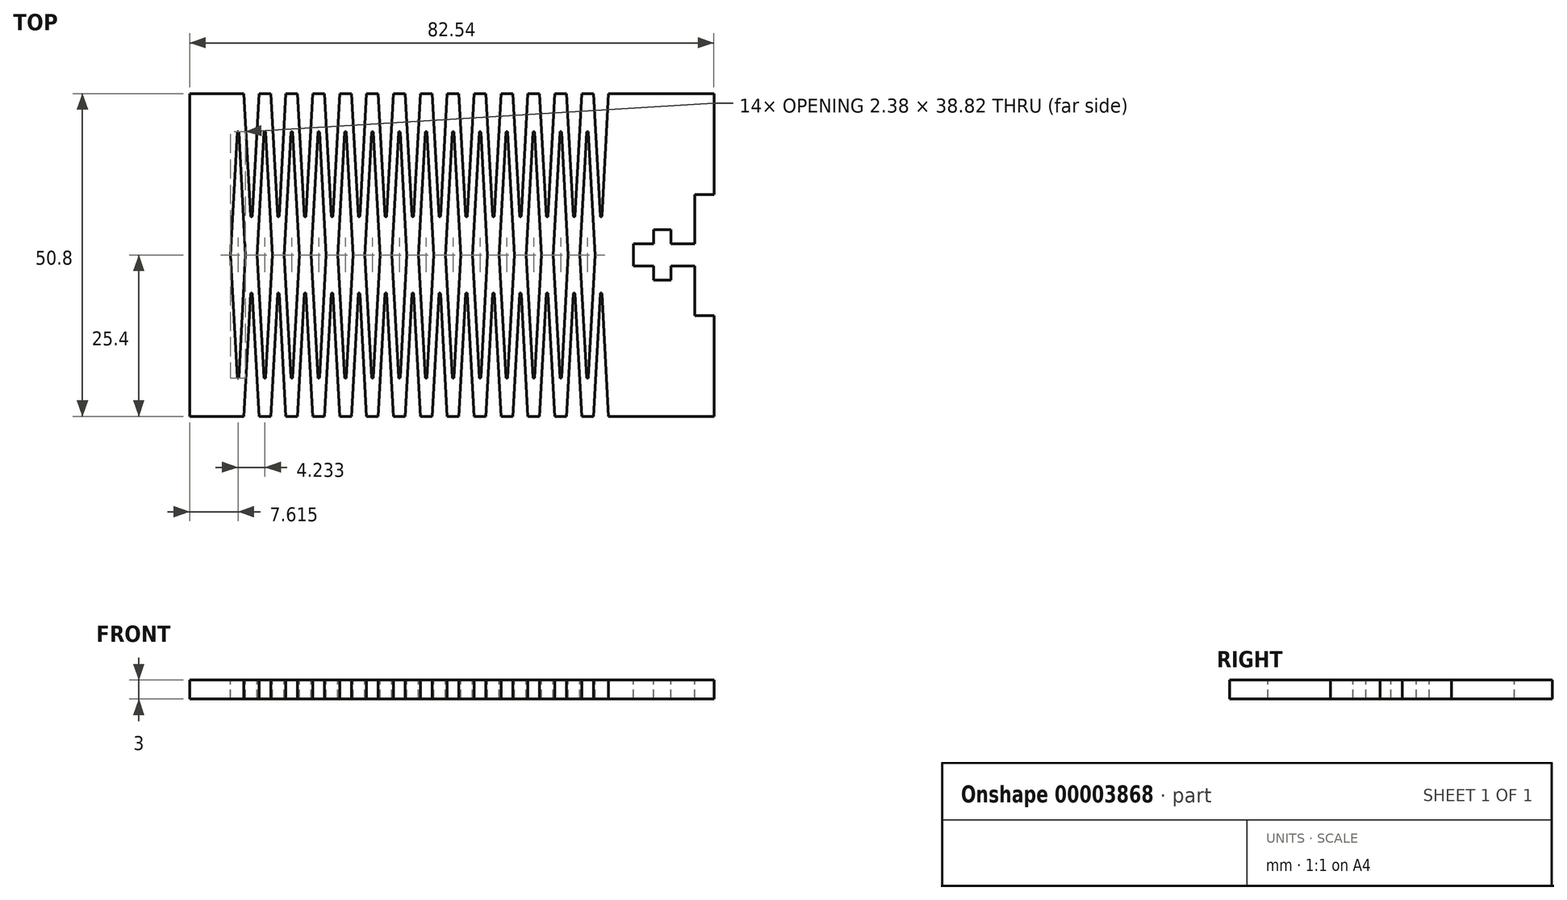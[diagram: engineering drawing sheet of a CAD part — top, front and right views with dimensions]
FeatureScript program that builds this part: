
annotation { "Feature Type Name" : "Feature", "Feature Type Description" : "" }
export const myFeature = defineFeature(function(context is Context, id is Id, definition is map)
    precondition{}
    {
        {
            var Q0;
            Q0=qCreatedBy(makeId("Top.planeOp"),FACE);
            var sketch = newSketch(context, id + "F0", { "sketchPlane" : qUnion([Q0])});
            skLineSegment(sketch, "E0.rect.bottom", {"start": v(41.28, 25.4) * mm, "end": v(-41.28, 25.4) * mm});
            skLineSegment(sketch, "E0.rect.top", {"start": v(41.28, -25.4) * mm, "end": v(-41.28, -25.4) * mm});
            skLineSegment(sketch, "E0.rect.left", {"start": v(41.28, 25.4) * mm, "end": v(41.28, -25.4) * mm});
            skLineSegment(sketch, "E0.rect.right", {"start": v(-41.28, 25.4) * mm, "end": v(-41.28, -25.4) * mm});
            skPoint(sketch, "E0.rect.middle", {"position": v(0, 0) * mm});
            skSolve(sketch);
        }
        {
            var Q0;
            Q0=makeQuery(id+"F0.imprint","IMPRINT",FACE,{"disambiguationData":[TD([[makeQuery(id+"F0.imprint","IMPRINT",EDGE,{"derivedFrom":sQuery(id+"F0.wireOp",EDGE,"E0.rect.bottom")}),1.0]])]});
            extrude(context, id + "F1", {"entities" : qUnion([Q0]), "depth" : 3 * mm});
        }
        {
            var Q0;
            Q0=makeQuery(id+"F1.opExtrude","CAP_FACE",FACE,{"disambiguationData":[OSD([sQuery(id+"F0.wireOp",EDGE,"E0.rect.bottom"),sQuery(id+"F0.wireOp",EDGE,"E0.rect.top"),sQuery(id+"F0.wireOp",EDGE,"E0.rect.left"),sQuery(id+"F0.wireOp",EDGE,"E0.rect.right")])],"isStart":false});
            var sketch = newSketch(context, id + "F2", { "sketchPlane" : qUnion([Q0])});
            skLineSegment(sketch, "E1.rect.bottom", {"start": v(38.28, 9.53) * mm, "end": v(41.28, 9.53) * mm});
            skLineSegment(sketch, "E1.rect.top", {"start": v(38.28, -9.53) * mm, "end": v(41.28, -9.53) * mm});
            skLineSegment(sketch, "E1.rect.right", {"start": v(41.28, 9.52) * mm, "end": v(41.28, -9.53) * mm});
            skPoint(sketch, "E1.rect.middle", {"position": v(39.78, 0) * mm});
            skLineSegment(sketch, "E2", {"start": v(38.28, 9.53) * mm, "end": v(38.28, 1.75) * mm});
            skLineSegment(sketch, "E3", {"start": v(38.28, 1.75) * mm, "end": v(34.53, 1.75) * mm});
            skLineSegment(sketch, "E4", {"start": v(34.53, 1.75) * mm, "end": v(34.53, 3.97) * mm});
            skLineSegment(sketch, "E5", {"start": v(34.53, 3.97) * mm, "end": v(31.75, 3.97) * mm});
            skLineSegment(sketch, "E6", {"start": v(31.75, 3.97) * mm, "end": v(31.75, 1.75) * mm});
            skLineSegment(sketch, "E7", {"start": v(31.75, 1.75) * mm, "end": v(28.58, 1.75) * mm});
            skLineSegment(sketch, "E8", {"start": v(28.58, 1.75) * mm, "end": v(28.58, 0) * mm});
            skLineSegment(sketch, "E9", {"start": v(41.28, 0) * mm, "end": v(11.15, 0) * mm, "construction": true});
            skLineSegment(sketch, "E10.0.MirrorCS", {"start": v(38.28, -9.53) * mm, "end": v(38.28, -1.75) * mm});
            skLineSegment(sketch, "E11.0.MirrorCS", {"start": v(38.28, -1.75) * mm, "end": v(34.53, -1.75) * mm});
            skLineSegment(sketch, "E12.0.MirrorCS", {"start": v(34.53, -1.75) * mm, "end": v(34.53, -3.97) * mm});
            skLineSegment(sketch, "E13.0.MirrorCS", {"start": v(34.53, -3.97) * mm, "end": v(31.75, -3.97) * mm});
            skLineSegment(sketch, "E14.0.MirrorCS", {"start": v(31.75, -3.97) * mm, "end": v(31.75, -1.75) * mm});
            skLineSegment(sketch, "E15.0.MirrorCS", {"start": v(31.75, -1.75) * mm, "end": v(28.58, -1.75) * mm});
            skLineSegment(sketch, "E16.0.MirrorCS", {"start": v(28.58, -1.75) * mm, "end": v(28.58, 0) * mm});
            skLineSegment(sketch, "E17", {"start": v(23.62, 6.1) * mm, "end": v(24.69, 25.4) * mm});
            skLineSegment(sketch, "E18", {"start": v(24.69, 25.4) * mm, "end": v(22.3, 25.4) * mm});
            skLineSegment(sketch, "E19", {"start": v(22.3, 25.4) * mm, "end": v(23.37, 6.1) * mm});
            skPoint(sketch, "E20.visualSharp", {"position": v(23.5, 3.81) * mm});
            skArc(sketch, "E20.filletArc", {"start": v(23.37, 6.1) * mm, "mid": v(23.5, 5.99) * mm, "end": v(23.62, 6.1) * mm});
            skLineSegment(sketch, "E21.0.MirrorCS", {"start": v(22.3, -25.4) * mm, "end": v(23.37, -6.1) * mm});
            skLineSegment(sketch, "E22.0.MirrorCS", {"start": v(23.62, -6.1) * mm, "end": v(24.69, -25.4) * mm});
            skLineSegment(sketch, "E23.0.MirrorCS", {"start": v(24.69, -25.4) * mm, "end": v(22.3, -25.4) * mm});
            skArc(sketch, "E24.0.MirrorCS", {"start": v(23.37, -6.1) * mm, "mid": v(23.5, -5.99) * mm, "end": v(23.62, -6.1) * mm});
            skLineSegment(sketch, "E25.1.0.0", {"start": v(18.07, 25.4) * mm, "end": v(19.13, 6.1) * mm});
            skLineSegment(sketch, "E25.1.0.1", {"start": v(19.39, 6.1) * mm, "end": v(20.45, 25.4) * mm});
            skLineSegment(sketch, "E25.1.0.2", {"start": v(20.45, 25.4) * mm, "end": v(18.07, 25.4) * mm});
            skLineSegment(sketch, "E25.1.0.3", {"start": v(18.07, -25.4) * mm, "end": v(19.13, -6.1) * mm});
            skLineSegment(sketch, "E25.1.0.4", {"start": v(19.39, -6.1) * mm, "end": v(20.45, -25.4) * mm});
            skLineSegment(sketch, "E25.1.0.5", {"start": v(20.45, -25.4) * mm, "end": v(18.07, -25.4) * mm});
            skArc(sketch, "E25.1.0.6", {"start": v(19.13, -6.1) * mm, "mid": v(19.26, -5.99) * mm, "end": v(19.39, -6.1) * mm});
            skArc(sketch, "E25.1.0.7", {"start": v(19.13, 6.1) * mm, "mid": v(19.26, 5.99) * mm, "end": v(19.39, 6.1) * mm});
            skLineSegment(sketch, "E25.2.0.0", {"start": v(13.84, 25.4) * mm, "end": v(14.9, 6.1) * mm});
            skLineSegment(sketch, "E25.2.0.1", {"start": v(15.16, 6.1) * mm, "end": v(16.22, 25.4) * mm});
            skLineSegment(sketch, "E25.2.0.2", {"start": v(16.22, 25.4) * mm, "end": v(13.84, 25.4) * mm});
            skLineSegment(sketch, "E25.2.0.3", {"start": v(13.84, -25.4) * mm, "end": v(14.9, -6.1) * mm});
            skLineSegment(sketch, "E25.2.0.4", {"start": v(15.16, -6.1) * mm, "end": v(16.22, -25.4) * mm});
            skLineSegment(sketch, "E25.2.0.5", {"start": v(16.22, -25.4) * mm, "end": v(13.84, -25.4) * mm});
            skArc(sketch, "E25.2.0.6", {"start": v(14.9, -6.1) * mm, "mid": v(15.03, -5.99) * mm, "end": v(15.16, -6.1) * mm});
            skArc(sketch, "E25.2.0.7", {"start": v(14.9, 6.1) * mm, "mid": v(15.03, 5.99) * mm, "end": v(15.16, 6.1) * mm});
            skLineSegment(sketch, "E25.direction1", {"start": v(23.37, 6.1) * mm, "end": v(19.13, 6.1) * mm, "construction": true});
            skLineSegment(sketch, "E26.0.3.0", {"start": v(9.6, 25.4) * mm, "end": v(10.67, 6.1) * mm});
            skLineSegment(sketch, "E26.3.3.0", {"start": v(10.92, 6.1) * mm, "end": v(11.99, 25.4) * mm});
            skLineSegment(sketch, "E26.6.3.0", {"start": v(11.99, 25.4) * mm, "end": v(9.6, 25.4) * mm});
            skLineSegment(sketch, "E26.9.3.0", {"start": v(9.6, -25.4) * mm, "end": v(10.67, -6.1) * mm});
            skLineSegment(sketch, "E26.12.3.0", {"start": v(10.92, -6.1) * mm, "end": v(11.99, -25.4) * mm});
            skLineSegment(sketch, "E26.15.3.0", {"start": v(11.99, -25.4) * mm, "end": v(9.6, -25.4) * mm});
            skArc(sketch, "E26.18.3.0", {"start": v(10.67, -6.1) * mm, "mid": v(10.8, -5.99) * mm, "end": v(10.92, -6.1) * mm});
            skArc(sketch, "E26.22.3.0", {"start": v(10.67, 6.1) * mm, "mid": v(10.8, 5.99) * mm, "end": v(10.92, 6.1) * mm});
            skLineSegment(sketch, "E26.0.4.0", {"start": v(5.37, 25.4) * mm, "end": v(6.43, 6.1) * mm});
            skLineSegment(sketch, "E26.3.4.0", {"start": v(6.69, 6.1) * mm, "end": v(7.75, 25.4) * mm});
            skLineSegment(sketch, "E26.6.4.0", {"start": v(7.75, 25.4) * mm, "end": v(5.37, 25.4) * mm});
            skLineSegment(sketch, "E26.9.4.0", {"start": v(5.37, -25.4) * mm, "end": v(6.43, -6.1) * mm});
            skLineSegment(sketch, "E26.12.4.0", {"start": v(6.69, -6.1) * mm, "end": v(7.75, -25.4) * mm});
            skLineSegment(sketch, "E26.15.4.0", {"start": v(7.75, -25.4) * mm, "end": v(5.37, -25.4) * mm});
            skArc(sketch, "E26.18.4.0", {"start": v(6.43, -6.1) * mm, "mid": v(6.56, -5.99) * mm, "end": v(6.69, -6.1) * mm});
            skArc(sketch, "E26.22.4.0", {"start": v(6.43, 6.1) * mm, "mid": v(6.56, 5.99) * mm, "end": v(6.69, 6.1) * mm});
            skLineSegment(sketch, "E26.0.5.0", {"start": v(1.14, 25.4) * mm, "end": v(2.2, 6.1) * mm});
            skLineSegment(sketch, "E26.3.5.0", {"start": v(2.46, 6.1) * mm, "end": v(3.52, 25.4) * mm});
            skLineSegment(sketch, "E26.6.5.0", {"start": v(3.52, 25.4) * mm, "end": v(1.14, 25.4) * mm});
            skLineSegment(sketch, "E26.9.5.0", {"start": v(1.14, -25.4) * mm, "end": v(2.2, -6.1) * mm});
            skLineSegment(sketch, "E26.12.5.0", {"start": v(2.46, -6.1) * mm, "end": v(3.52, -25.4) * mm});
            skLineSegment(sketch, "E26.15.5.0", {"start": v(3.52, -25.4) * mm, "end": v(1.14, -25.4) * mm});
            skArc(sketch, "E26.18.5.0", {"start": v(2.2, -6.1) * mm, "mid": v(2.33, -5.99) * mm, "end": v(2.46, -6.1) * mm});
            skArc(sketch, "E26.22.5.0", {"start": v(2.2, 6.1) * mm, "mid": v(2.33, 5.99) * mm, "end": v(2.46, 6.1) * mm});
            skLineSegment(sketch, "E26.0.6.0", {"start": v(-3.1, 25.4) * mm, "end": v(-2.03, 6.1) * mm});
            skLineSegment(sketch, "E26.3.6.0", {"start": v(-1.78, 6.1) * mm, "end": v(-0.71, 25.4) * mm});
            skLineSegment(sketch, "E26.6.6.0", {"start": v(-0.71, 25.4) * mm, "end": v(-3.1, 25.4) * mm});
            skLineSegment(sketch, "E26.9.6.0", {"start": v(-3.1, -25.4) * mm, "end": v(-2.03, -6.1) * mm});
            skLineSegment(sketch, "E26.12.6.0", {"start": v(-1.78, -6.1) * mm, "end": v(-0.71, -25.4) * mm});
            skLineSegment(sketch, "E26.15.6.0", {"start": v(-0.71, -25.4) * mm, "end": v(-3.1, -25.4) * mm});
            skArc(sketch, "E26.18.6.0", {"start": v(-2.03, -6.1) * mm, "mid": v(-1.9, -5.99) * mm, "end": v(-1.78, -6.1) * mm});
            skArc(sketch, "E26.22.6.0", {"start": v(-2.03, 6.1) * mm, "mid": v(-1.9, 5.99) * mm, "end": v(-1.78, 6.1) * mm});
            skLineSegment(sketch, "E26.0.7.0", {"start": v(-7.33, 25.4) * mm, "end": v(-6.27, 6.1) * mm});
            skLineSegment(sketch, "E26.3.7.0", {"start": v(-6.01, 6.1) * mm, "end": v(-4.95, 25.4) * mm});
            skLineSegment(sketch, "E26.6.7.0", {"start": v(-4.95, 25.4) * mm, "end": v(-7.33, 25.4) * mm});
            skLineSegment(sketch, "E26.9.7.0", {"start": v(-7.33, -25.4) * mm, "end": v(-6.27, -6.1) * mm});
            skLineSegment(sketch, "E26.12.7.0", {"start": v(-6.01, -6.1) * mm, "end": v(-4.95, -25.4) * mm});
            skLineSegment(sketch, "E26.15.7.0", {"start": v(-4.95, -25.4) * mm, "end": v(-7.33, -25.4) * mm});
            skArc(sketch, "E26.18.7.0", {"start": v(-6.27, -6.1) * mm, "mid": v(-6.14, -5.99) * mm, "end": v(-6.01, -6.1) * mm});
            skArc(sketch, "E26.22.7.0", {"start": v(-6.27, 6.1) * mm, "mid": v(-6.14, 5.99) * mm, "end": v(-6.01, 6.1) * mm});
            skLineSegment(sketch, "E26.0.8.0", {"start": v(-11.56, 25.4) * mm, "end": v(-10.5, 6.1) * mm});
            skLineSegment(sketch, "E26.3.8.0", {"start": v(-10.24, 6.1) * mm, "end": v(-9.18, 25.4) * mm});
            skLineSegment(sketch, "E26.6.8.0", {"start": v(-9.18, 25.4) * mm, "end": v(-11.56, 25.4) * mm});
            skLineSegment(sketch, "E26.9.8.0", {"start": v(-11.56, -25.4) * mm, "end": v(-10.5, -6.1) * mm});
            skLineSegment(sketch, "E26.12.8.0", {"start": v(-10.24, -6.1) * mm, "end": v(-9.18, -25.4) * mm});
            skLineSegment(sketch, "E26.15.8.0", {"start": v(-9.18, -25.4) * mm, "end": v(-11.56, -25.4) * mm});
            skArc(sketch, "E26.18.8.0", {"start": v(-10.5, -6.1) * mm, "mid": v(-10.37, -5.99) * mm, "end": v(-10.24, -6.1) * mm});
            skArc(sketch, "E26.22.8.0", {"start": v(-10.5, 6.1) * mm, "mid": v(-10.37, 5.99) * mm, "end": v(-10.24, 6.1) * mm});
            skLineSegment(sketch, "E26.0.9.0", {"start": v(-15.8, 25.4) * mm, "end": v(-14.73, 6.1) * mm});
            skLineSegment(sketch, "E26.3.9.0", {"start": v(-14.48, 6.1) * mm, "end": v(-13.41, 25.4) * mm});
            skLineSegment(sketch, "E26.6.9.0", {"start": v(-13.41, 25.4) * mm, "end": v(-15.8, 25.4) * mm});
            skLineSegment(sketch, "E26.9.9.0", {"start": v(-15.8, -25.4) * mm, "end": v(-14.73, -6.1) * mm});
            skLineSegment(sketch, "E26.12.9.0", {"start": v(-14.48, -6.1) * mm, "end": v(-13.41, -25.4) * mm});
            skLineSegment(sketch, "E26.15.9.0", {"start": v(-13.41, -25.4) * mm, "end": v(-15.8, -25.4) * mm});
            skArc(sketch, "E26.18.9.0", {"start": v(-14.73, -6.1) * mm, "mid": v(-14.6, -5.99) * mm, "end": v(-14.48, -6.1) * mm});
            skArc(sketch, "E26.22.9.0", {"start": v(-14.73, 6.1) * mm, "mid": v(-14.6, 5.99) * mm, "end": v(-14.48, 6.1) * mm});
            skLineSegment(sketch, "E27.0.10.0", {"start": v(-20.03, 25.4) * mm, "end": v(-18.97, 6.1) * mm});
            skLineSegment(sketch, "E27.3.10.0", {"start": v(-18.71, 6.1) * mm, "end": v(-17.65, 25.4) * mm});
            skLineSegment(sketch, "E27.6.10.0", {"start": v(-17.65, 25.4) * mm, "end": v(-20.03, 25.4) * mm});
            skLineSegment(sketch, "E27.9.10.0", {"start": v(-20.03, -25.4) * mm, "end": v(-18.97, -6.1) * mm});
            skLineSegment(sketch, "E27.12.10.0", {"start": v(-18.71, -6.1) * mm, "end": v(-17.65, -25.4) * mm});
            skLineSegment(sketch, "E27.15.10.0", {"start": v(-17.65, -25.4) * mm, "end": v(-20.03, -25.4) * mm});
            skArc(sketch, "E27.18.10.0", {"start": v(-18.97, -6.1) * mm, "mid": v(-18.84, -5.99) * mm, "end": v(-18.71, -6.1) * mm});
            skArc(sketch, "E27.22.10.0", {"start": v(-18.97, 6.1) * mm, "mid": v(-18.84, 5.99) * mm, "end": v(-18.71, 6.1) * mm});
            skLineSegment(sketch, "E27.0.11.0", {"start": v(-24.26, 25.4) * mm, "end": v(-23.2, 6.1) * mm});
            skLineSegment(sketch, "E27.3.11.0", {"start": v(-22.94, 6.1) * mm, "end": v(-21.88, 25.4) * mm});
            skLineSegment(sketch, "E27.6.11.0", {"start": v(-21.88, 25.4) * mm, "end": v(-24.26, 25.4) * mm});
            skLineSegment(sketch, "E27.9.11.0", {"start": v(-24.26, -25.4) * mm, "end": v(-23.2, -6.1) * mm});
            skLineSegment(sketch, "E27.12.11.0", {"start": v(-22.94, -6.1) * mm, "end": v(-21.88, -25.4) * mm});
            skLineSegment(sketch, "E27.15.11.0", {"start": v(-21.88, -25.4) * mm, "end": v(-24.26, -25.4) * mm});
            skArc(sketch, "E27.18.11.0", {"start": v(-23.2, -6.1) * mm, "mid": v(-23.07, -5.99) * mm, "end": v(-22.94, -6.1) * mm});
            skArc(sketch, "E27.22.11.0", {"start": v(-23.2, 6.1) * mm, "mid": v(-23.07, 5.99) * mm, "end": v(-22.94, 6.1) * mm});
            skLineSegment(sketch, "E27.0.12.0", {"start": v(-28.5, 25.4) * mm, "end": v(-27.43, 6.1) * mm});
            skLineSegment(sketch, "E27.3.12.0", {"start": v(-27.18, 6.1) * mm, "end": v(-26.11, 25.4) * mm});
            skLineSegment(sketch, "E27.6.12.0", {"start": v(-26.11, 25.4) * mm, "end": v(-28.5, 25.4) * mm});
            skLineSegment(sketch, "E27.9.12.0", {"start": v(-28.5, -25.4) * mm, "end": v(-27.43, -6.1) * mm});
            skLineSegment(sketch, "E27.12.12.0", {"start": v(-27.18, -6.1) * mm, "end": v(-26.11, -25.4) * mm});
            skLineSegment(sketch, "E27.15.12.0", {"start": v(-26.11, -25.4) * mm, "end": v(-28.5, -25.4) * mm});
            skArc(sketch, "E27.18.12.0", {"start": v(-27.43, -6.1) * mm, "mid": v(-27.3, -5.99) * mm, "end": v(-27.18, -6.1) * mm});
            skArc(sketch, "E27.22.12.0", {"start": v(-27.43, 6.1) * mm, "mid": v(-27.3, 5.99) * mm, "end": v(-27.18, 6.1) * mm});
            skLineSegment(sketch, "E27.0.13.0", {"start": v(-32.73, 25.4) * mm, "end": v(-31.67, 6.1) * mm});
            skLineSegment(sketch, "E27.3.13.0", {"start": v(-31.41, 6.1) * mm, "end": v(-30.35, 25.4) * mm});
            skLineSegment(sketch, "E27.6.13.0", {"start": v(-30.35, 25.4) * mm, "end": v(-32.73, 25.4) * mm});
            skLineSegment(sketch, "E27.9.13.0", {"start": v(-32.73, -25.4) * mm, "end": v(-31.67, -6.1) * mm});
            skLineSegment(sketch, "E27.12.13.0", {"start": v(-31.41, -6.1) * mm, "end": v(-30.35, -25.4) * mm});
            skLineSegment(sketch, "E27.15.13.0", {"start": v(-30.35, -25.4) * mm, "end": v(-32.73, -25.4) * mm});
            skArc(sketch, "E27.18.13.0", {"start": v(-31.67, -6.1) * mm, "mid": v(-31.54, -5.99) * mm, "end": v(-31.41, -6.1) * mm});
            skArc(sketch, "E27.22.13.0", {"start": v(-31.67, 6.1) * mm, "mid": v(-31.54, 5.99) * mm, "end": v(-31.41, 6.1) * mm});
            skLineSegment(sketch, "E28", {"start": v(21.5, 19.3) * mm, "end": v(22.57, 0) * mm});
            skLineSegment(sketch, "E29", {"start": v(20.19, 0) * mm, "end": v(21.25, 19.3) * mm});
            skPoint(sketch, "E30.visualSharp", {"position": v(21.38, 21.59) * mm});
            skArc(sketch, "E30.filletArc", {"start": v(21.5, 19.3) * mm, "mid": v(21.38, 19.41) * mm, "end": v(21.25, 19.3) * mm});
            skLineSegment(sketch, "E31.0.MirrorCS", {"start": v(20.19, 0) * mm, "end": v(21.25, -19.3) * mm});
            skLineSegment(sketch, "E32.0.MirrorCS", {"start": v(21.5, -19.3) * mm, "end": v(22.57, 0) * mm});
            skArc(sketch, "E33.0.MirrorCS", {"start": v(21.5, -19.3) * mm, "mid": v(21.38, -19.41) * mm, "end": v(21.25, -19.3) * mm});
            skLineSegment(sketch, "E34.1.0.0", {"start": v(15.95, 0) * mm, "end": v(17.02, -19.3) * mm});
            skLineSegment(sketch, "E34.1.0.1", {"start": v(17.27, -19.3) * mm, "end": v(18.34, 0) * mm});
            skLineSegment(sketch, "E34.1.0.2", {"start": v(15.95, 0) * mm, "end": v(17.02, 19.3) * mm});
            skLineSegment(sketch, "E34.1.0.3", {"start": v(17.27, 19.3) * mm, "end": v(18.34, 0) * mm});
            skArc(sketch, "E34.1.0.4", {"start": v(17.27, 19.3) * mm, "mid": v(17.15, 19.41) * mm, "end": v(17.02, 19.3) * mm});
            skArc(sketch, "E34.1.0.5", {"start": v(17.27, -19.3) * mm, "mid": v(17.15, -19.41) * mm, "end": v(17.02, -19.3) * mm});
            skLineSegment(sketch, "E34.2.0.0", {"start": v(11.72, 0) * mm, "end": v(12.78, -19.3) * mm});
            skLineSegment(sketch, "E34.2.0.1", {"start": v(13.04, -19.3) * mm, "end": v(14.1, 0) * mm});
            skLineSegment(sketch, "E34.2.0.2", {"start": v(11.72, 0) * mm, "end": v(12.78, 19.3) * mm});
            skLineSegment(sketch, "E34.2.0.3", {"start": v(13.04, 19.3) * mm, "end": v(14.1, 0) * mm});
            skArc(sketch, "E34.2.0.4", {"start": v(13.04, 19.3) * mm, "mid": v(12.91, 19.41) * mm, "end": v(12.78, 19.3) * mm});
            skArc(sketch, "E34.2.0.5", {"start": v(13.04, -19.3) * mm, "mid": v(12.91, -19.41) * mm, "end": v(12.78, -19.3) * mm});
            skLineSegment(sketch, "E34.direction1", {"start": v(21.25, -19.3) * mm, "end": v(17.02, -19.3) * mm, "construction": true});
            skLineSegment(sketch, "E35.0.3.0", {"start": v(7.49, 0) * mm, "end": v(8.55, -19.3) * mm});
            skLineSegment(sketch, "E35.3.3.0", {"start": v(8.8, -19.3) * mm, "end": v(9.87, 0) * mm});
            skLineSegment(sketch, "E35.6.3.0", {"start": v(7.49, 0) * mm, "end": v(8.55, 19.3) * mm});
            skLineSegment(sketch, "E35.9.3.0", {"start": v(8.8, 19.3) * mm, "end": v(9.87, 0) * mm});
            skArc(sketch, "E35.12.3.0", {"start": v(8.8, 19.3) * mm, "mid": v(8.68, 19.41) * mm, "end": v(8.55, 19.3) * mm});
            skArc(sketch, "E35.16.3.0", {"start": v(8.8, -19.3) * mm, "mid": v(8.68, -19.41) * mm, "end": v(8.55, -19.3) * mm});
            skLineSegment(sketch, "E35.0.4.0", {"start": v(3.25, 0) * mm, "end": v(4.32, -19.3) * mm});
            skLineSegment(sketch, "E35.3.4.0", {"start": v(4.57, -19.3) * mm, "end": v(5.64, 0) * mm});
            skLineSegment(sketch, "E35.6.4.0", {"start": v(3.25, 0) * mm, "end": v(4.32, 19.3) * mm});
            skLineSegment(sketch, "E35.9.4.0", {"start": v(4.57, 19.3) * mm, "end": v(5.64, 0) * mm});
            skArc(sketch, "E35.12.4.0", {"start": v(4.57, 19.3) * mm, "mid": v(4.45, 19.41) * mm, "end": v(4.32, 19.3) * mm});
            skArc(sketch, "E35.16.4.0", {"start": v(4.57, -19.3) * mm, "mid": v(4.45, -19.41) * mm, "end": v(4.32, -19.3) * mm});
            skLineSegment(sketch, "E35.0.5.0", {"start": v(-0.98, 0) * mm, "end": v(0.08, -19.3) * mm});
            skLineSegment(sketch, "E35.3.5.0", {"start": v(0.34, -19.3) * mm, "end": v(1.4, 0) * mm});
            skLineSegment(sketch, "E35.6.5.0", {"start": v(-0.98, 0) * mm, "end": v(0.08, 19.3) * mm});
            skLineSegment(sketch, "E35.9.5.0", {"start": v(0.34, 19.3) * mm, "end": v(1.4, 0) * mm});
            skArc(sketch, "E35.12.5.0", {"start": v(0.34, 19.3) * mm, "mid": v(0.21, 19.41) * mm, "end": v(0.08, 19.3) * mm});
            skArc(sketch, "E35.16.5.0", {"start": v(0.34, -19.3) * mm, "mid": v(0.21, -19.41) * mm, "end": v(0.08, -19.3) * mm});
            skLineSegment(sketch, "E35.0.6.0", {"start": v(-5.21, 0) * mm, "end": v(-4.15, -19.3) * mm});
            skLineSegment(sketch, "E35.3.6.0", {"start": v(-3.9, -19.3) * mm, "end": v(-2.83, 0) * mm});
            skLineSegment(sketch, "E35.6.6.0", {"start": v(-5.21, 0) * mm, "end": v(-4.15, 19.3) * mm});
            skLineSegment(sketch, "E35.9.6.0", {"start": v(-3.9, 19.3) * mm, "end": v(-2.83, 0) * mm});
            skArc(sketch, "E35.12.6.0", {"start": v(-3.9, 19.3) * mm, "mid": v(-4.02, 19.41) * mm, "end": v(-4.15, 19.3) * mm});
            skArc(sketch, "E35.16.6.0", {"start": v(-3.9, -19.3) * mm, "mid": v(-4.02, -19.41) * mm, "end": v(-4.15, -19.3) * mm});
            skLineSegment(sketch, "E35.0.7.0", {"start": v(-9.45, 0) * mm, "end": v(-8.38, -19.3) * mm});
            skLineSegment(sketch, "E35.3.7.0", {"start": v(-8.13, -19.3) * mm, "end": v(-7.06, 0) * mm});
            skLineSegment(sketch, "E35.6.7.0", {"start": v(-9.45, 0) * mm, "end": v(-8.38, 19.3) * mm});
            skLineSegment(sketch, "E35.9.7.0", {"start": v(-8.13, 19.3) * mm, "end": v(-7.06, 0) * mm});
            skArc(sketch, "E35.12.7.0", {"start": v(-8.13, 19.3) * mm, "mid": v(-8.25, 19.41) * mm, "end": v(-8.38, 19.3) * mm});
            skArc(sketch, "E35.16.7.0", {"start": v(-8.13, -19.3) * mm, "mid": v(-8.25, -19.41) * mm, "end": v(-8.38, -19.3) * mm});
            skLineSegment(sketch, "E35.0.8.0", {"start": v(-13.68, 0) * mm, "end": v(-12.62, -19.3) * mm});
            skLineSegment(sketch, "E35.3.8.0", {"start": v(-12.36, -19.3) * mm, "end": v(-11.3, 0) * mm});
            skLineSegment(sketch, "E35.6.8.0", {"start": v(-13.68, 0) * mm, "end": v(-12.62, 19.3) * mm});
            skLineSegment(sketch, "E35.9.8.0", {"start": v(-12.36, 19.3) * mm, "end": v(-11.3, 0) * mm});
            skArc(sketch, "E35.12.8.0", {"start": v(-12.36, 19.3) * mm, "mid": v(-12.49, 19.41) * mm, "end": v(-12.62, 19.3) * mm});
            skArc(sketch, "E35.16.8.0", {"start": v(-12.36, -19.3) * mm, "mid": v(-12.49, -19.41) * mm, "end": v(-12.62, -19.3) * mm});
            skLineSegment(sketch, "E35.0.9.0", {"start": v(-17.91, 0) * mm, "end": v(-16.85, -19.3) * mm});
            skLineSegment(sketch, "E35.3.9.0", {"start": v(-16.6, -19.3) * mm, "end": v(-15.53, 0) * mm});
            skLineSegment(sketch, "E35.6.9.0", {"start": v(-17.91, 0) * mm, "end": v(-16.85, 19.3) * mm});
            skLineSegment(sketch, "E35.9.9.0", {"start": v(-16.6, 19.3) * mm, "end": v(-15.53, 0) * mm});
            skArc(sketch, "E35.12.9.0", {"start": v(-16.6, 19.3) * mm, "mid": v(-16.72, 19.41) * mm, "end": v(-16.85, 19.3) * mm});
            skArc(sketch, "E35.16.9.0", {"start": v(-16.6, -19.3) * mm, "mid": v(-16.72, -19.41) * mm, "end": v(-16.85, -19.3) * mm});
            skLineSegment(sketch, "E35.0.10.0", {"start": v(-22.15, 0) * mm, "end": v(-21.08, -19.3) * mm});
            skLineSegment(sketch, "E35.3.10.0", {"start": v(-20.83, -19.3) * mm, "end": v(-19.76, 0) * mm});
            skLineSegment(sketch, "E35.6.10.0", {"start": v(-22.15, 0) * mm, "end": v(-21.08, 19.3) * mm});
            skLineSegment(sketch, "E35.9.10.0", {"start": v(-20.83, 19.3) * mm, "end": v(-19.76, 0) * mm});
            skArc(sketch, "E35.12.10.0", {"start": v(-20.83, 19.3) * mm, "mid": v(-20.95, 19.41) * mm, "end": v(-21.08, 19.3) * mm});
            skArc(sketch, "E35.16.10.0", {"start": v(-20.83, -19.3) * mm, "mid": v(-20.95, -19.41) * mm, "end": v(-21.08, -19.3) * mm});
            skLineSegment(sketch, "E35.0.11.0", {"start": v(-26.38, 0) * mm, "end": v(-25.32, -19.3) * mm});
            skLineSegment(sketch, "E35.3.11.0", {"start": v(-25.06, -19.3) * mm, "end": v(-24, 0) * mm});
            skLineSegment(sketch, "E35.6.11.0", {"start": v(-26.38, 0) * mm, "end": v(-25.32, 19.3) * mm});
            skLineSegment(sketch, "E35.9.11.0", {"start": v(-25.06, 19.3) * mm, "end": v(-24, 0) * mm});
            skArc(sketch, "E35.12.11.0", {"start": v(-25.06, 19.3) * mm, "mid": v(-25.19, 19.41) * mm, "end": v(-25.32, 19.3) * mm});
            skArc(sketch, "E35.16.11.0", {"start": v(-25.06, -19.3) * mm, "mid": v(-25.19, -19.41) * mm, "end": v(-25.32, -19.3) * mm});
            skLineSegment(sketch, "E35.0.12.0", {"start": v(-30.61, 0) * mm, "end": v(-29.55, -19.3) * mm});
            skLineSegment(sketch, "E35.3.12.0", {"start": v(-29.3, -19.3) * mm, "end": v(-28.23, 0) * mm});
            skLineSegment(sketch, "E35.6.12.0", {"start": v(-30.61, 0) * mm, "end": v(-29.55, 19.3) * mm});
            skLineSegment(sketch, "E35.9.12.0", {"start": v(-29.3, 19.3) * mm, "end": v(-28.23, 0) * mm});
            skArc(sketch, "E35.12.12.0", {"start": v(-29.3, 19.3) * mm, "mid": v(-29.42, 19.41) * mm, "end": v(-29.55, 19.3) * mm});
            skArc(sketch, "E35.16.12.0", {"start": v(-29.3, -19.3) * mm, "mid": v(-29.42, -19.41) * mm, "end": v(-29.55, -19.3) * mm});
            skLineSegment(sketch, "E35.0.13.0", {"start": v(-34.85, 0) * mm, "end": v(-33.78, -19.3) * mm});
            skLineSegment(sketch, "E35.3.13.0", {"start": v(-33.53, -19.3) * mm, "end": v(-32.46, 0) * mm});
            skLineSegment(sketch, "E35.6.13.0", {"start": v(-34.85, 0) * mm, "end": v(-33.78, 19.3) * mm});
            skLineSegment(sketch, "E35.9.13.0", {"start": v(-33.53, 19.3) * mm, "end": v(-32.46, 0) * mm});
            skArc(sketch, "E35.12.13.0", {"start": v(-33.53, 19.3) * mm, "mid": v(-33.65, 19.41) * mm, "end": v(-33.78, 19.3) * mm});
            skArc(sketch, "E35.16.13.0", {"start": v(-33.53, -19.3) * mm, "mid": v(-33.65, -19.41) * mm, "end": v(-33.78, -19.3) * mm});
            skSolve(sketch);
        }
        {
            var Q0;
            {Q0=qUnion([makeQuery(id+"F2.imprint","IMPRINT",FACE,{"disambiguationData":[TD([[makeQuery(id+"F2.imprint","IMPRINT",EDGE,{"derivedFrom":sQuery(id+"F2.wireOp",EDGE,"E1.rect.bottom")}),-1.0]])]}),makeQuery(id+"F2.imprint","IMPRINT",FACE,{"disambiguationData":[TD([[makeQuery(id+"F2.imprint","IMPRINT",EDGE,{"derivedFrom":sQuery(id+"F2.wireOp",EDGE,"E17")}),1.0]])]}),makeQuery(id+"F2.imprint","IMPRINT",FACE,{"disambiguationData":[TD([[makeQuery(id+"F2.imprint","IMPRINT",EDGE,{"derivedFrom":sQuery(id+"F2.wireOp",EDGE,"E21.0.MirrorCS")}),-1.0]])]}),makeQuery(id+"F2.imprint","IMPRINT",FACE,{"disambiguationData":[TD([[makeQuery(id+"F2.imprint","IMPRINT",EDGE,{"derivedFrom":sQuery(id+"F2.wireOp",EDGE,"E25.1.0.0")}),1.0]])]}),makeQuery(id+"F2.imprint","IMPRINT",FACE,{"disambiguationData":[TD([[makeQuery(id+"F2.imprint","IMPRINT",EDGE,{"derivedFrom":sQuery(id+"F2.wireOp",EDGE,"E25.1.0.3")}),-1.0]])]}),makeQuery(id+"F2.imprint","IMPRINT",FACE,{"disambiguationData":[TD([[makeQuery(id+"F2.imprint","IMPRINT",EDGE,{"derivedFrom":sQuery(id+"F2.wireOp",EDGE,"E25.2.0.0")}),1.0]])]}),makeQuery(id+"F2.imprint","IMPRINT",FACE,{"disambiguationData":[TD([[makeQuery(id+"F2.imprint","IMPRINT",EDGE,{"derivedFrom":sQuery(id+"F2.wireOp",EDGE,"E25.2.0.3")}),-1.0]])]}),makeQuery(id+"F2.imprint","IMPRINT",FACE,{"disambiguationData":[TD([[makeQuery(id+"F2.imprint","IMPRINT",EDGE,{"derivedFrom":sQuery(id+"F2.wireOp",EDGE,"E26.0.3.0")}),1.0]])]}),makeQuery(id+"F2.imprint","IMPRINT",FACE,{"disambiguationData":[TD([[makeQuery(id+"F2.imprint","IMPRINT",EDGE,{"derivedFrom":sQuery(id+"F2.wireOp",EDGE,"E26.9.3.0")}),-1.0]])]}),makeQuery(id+"F2.imprint","IMPRINT",FACE,{"disambiguationData":[TD([[makeQuery(id+"F2.imprint","IMPRINT",EDGE,{"derivedFrom":sQuery(id+"F2.wireOp",EDGE,"E26.0.4.0")}),1.0]])]}),makeQuery(id+"F2.imprint","IMPRINT",FACE,{"disambiguationData":[TD([[makeQuery(id+"F2.imprint","IMPRINT",EDGE,{"derivedFrom":sQuery(id+"F2.wireOp",EDGE,"E26.9.4.0")}),-1.0]])]}),makeQuery(id+"F2.imprint","IMPRINT",FACE,{"disambiguationData":[TD([[makeQuery(id+"F2.imprint","IMPRINT",EDGE,{"derivedFrom":sQuery(id+"F2.wireOp",EDGE,"E26.0.5.0")}),1.0]])]}),makeQuery(id+"F2.imprint","IMPRINT",FACE,{"disambiguationData":[TD([[makeQuery(id+"F2.imprint","IMPRINT",EDGE,{"derivedFrom":sQuery(id+"F2.wireOp",EDGE,"E26.9.5.0")}),-1.0]])]}),makeQuery(id+"F2.imprint","IMPRINT",FACE,{"disambiguationData":[TD([[makeQuery(id+"F2.imprint","IMPRINT",EDGE,{"derivedFrom":sQuery(id+"F2.wireOp",EDGE,"E26.0.6.0")}),1.0]])]}),makeQuery(id+"F2.imprint","IMPRINT",FACE,{"disambiguationData":[TD([[makeQuery(id+"F2.imprint","IMPRINT",EDGE,{"derivedFrom":sQuery(id+"F2.wireOp",EDGE,"E26.9.6.0")}),-1.0]])]}),makeQuery(id+"F2.imprint","IMPRINT",FACE,{"disambiguationData":[TD([[makeQuery(id+"F2.imprint","IMPRINT",EDGE,{"derivedFrom":sQuery(id+"F2.wireOp",EDGE,"E26.0.7.0")}),1.0]])]}),makeQuery(id+"F2.imprint","IMPRINT",FACE,{"disambiguationData":[TD([[makeQuery(id+"F2.imprint","IMPRINT",EDGE,{"derivedFrom":sQuery(id+"F2.wireOp",EDGE,"E26.9.7.0")}),-1.0]])]}),makeQuery(id+"F2.imprint","IMPRINT",FACE,{"disambiguationData":[TD([[makeQuery(id+"F2.imprint","IMPRINT",EDGE,{"derivedFrom":sQuery(id+"F2.wireOp",EDGE,"E26.0.8.0")}),1.0]])]}),makeQuery(id+"F2.imprint","IMPRINT",FACE,{"disambiguationData":[TD([[makeQuery(id+"F2.imprint","IMPRINT",EDGE,{"derivedFrom":sQuery(id+"F2.wireOp",EDGE,"E26.9.8.0")}),-1.0]])]}),makeQuery(id+"F2.imprint","IMPRINT",FACE,{"disambiguationData":[TD([[makeQuery(id+"F2.imprint","IMPRINT",EDGE,{"derivedFrom":sQuery(id+"F2.wireOp",EDGE,"E26.0.9.0")}),1.0]])]}),makeQuery(id+"F2.imprint","IMPRINT",FACE,{"disambiguationData":[TD([[makeQuery(id+"F2.imprint","IMPRINT",EDGE,{"derivedFrom":sQuery(id+"F2.wireOp",EDGE,"E26.9.9.0")}),-1.0]])]}),makeQuery(id+"F2.imprint","IMPRINT",FACE,{"disambiguationData":[TD([[makeQuery(id+"F2.imprint","IMPRINT",EDGE,{"derivedFrom":sQuery(id+"F2.wireOp",EDGE,"E27.0.10.0")}),1.0]])]}),makeQuery(id+"F2.imprint","IMPRINT",FACE,{"disambiguationData":[TD([[makeQuery(id+"F2.imprint","IMPRINT",EDGE,{"derivedFrom":sQuery(id+"F2.wireOp",EDGE,"E27.9.10.0")}),-1.0]])]}),makeQuery(id+"F2.imprint","IMPRINT",FACE,{"disambiguationData":[TD([[makeQuery(id+"F2.imprint","IMPRINT",EDGE,{"derivedFrom":sQuery(id+"F2.wireOp",EDGE,"E27.0.11.0")}),1.0]])]}),makeQuery(id+"F2.imprint","IMPRINT",FACE,{"disambiguationData":[TD([[makeQuery(id+"F2.imprint","IMPRINT",EDGE,{"derivedFrom":sQuery(id+"F2.wireOp",EDGE,"E27.9.11.0")}),-1.0]])]}),makeQuery(id+"F2.imprint","IMPRINT",FACE,{"disambiguationData":[TD([[makeQuery(id+"F2.imprint","IMPRINT",EDGE,{"derivedFrom":sQuery(id+"F2.wireOp",EDGE,"E27.0.12.0")}),1.0]])]}),makeQuery(id+"F2.imprint","IMPRINT",FACE,{"disambiguationData":[TD([[makeQuery(id+"F2.imprint","IMPRINT",EDGE,{"derivedFrom":sQuery(id+"F2.wireOp",EDGE,"E27.9.12.0")}),-1.0]])]}),makeQuery(id+"F2.imprint","IMPRINT",FACE,{"disambiguationData":[TD([[makeQuery(id+"F2.imprint","IMPRINT",EDGE,{"derivedFrom":sQuery(id+"F2.wireOp",EDGE,"E27.0.13.0")}),1.0]])]}),makeQuery(id+"F2.imprint","IMPRINT",FACE,{"disambiguationData":[TD([[makeQuery(id+"F2.imprint","IMPRINT",EDGE,{"derivedFrom":sQuery(id+"F2.wireOp",EDGE,"E27.9.13.0")}),-1.0]])]}),makeQuery(id+"F2.imprint","IMPRINT",FACE,{"disambiguationData":[TD([[makeQuery(id+"F2.imprint","IMPRINT",EDGE,{"derivedFrom":sQuery(id+"F2.wireOp",EDGE,"E28")}),-1.0]])]}),makeQuery(id+"F2.imprint","IMPRINT",FACE,{"disambiguationData":[TD([[makeQuery(id+"F2.imprint","IMPRINT",EDGE,{"derivedFrom":sQuery(id+"F2.wireOp",EDGE,"E34.1.0.0")}),1.0]])]}),makeQuery(id+"F2.imprint","IMPRINT",FACE,{"disambiguationData":[TD([[makeQuery(id+"F2.imprint","IMPRINT",EDGE,{"derivedFrom":sQuery(id+"F2.wireOp",EDGE,"E34.2.0.0")}),1.0]])]}),makeQuery(id+"F2.imprint","IMPRINT",FACE,{"disambiguationData":[TD([[makeQuery(id+"F2.imprint","IMPRINT",EDGE,{"derivedFrom":sQuery(id+"F2.wireOp",EDGE,"E35.0.3.0")}),1.0]])]}),makeQuery(id+"F2.imprint","IMPRINT",FACE,{"disambiguationData":[TD([[makeQuery(id+"F2.imprint","IMPRINT",EDGE,{"derivedFrom":sQuery(id+"F2.wireOp",EDGE,"E35.0.4.0")}),1.0]])]}),makeQuery(id+"F2.imprint","IMPRINT",FACE,{"disambiguationData":[TD([[makeQuery(id+"F2.imprint","IMPRINT",EDGE,{"derivedFrom":sQuery(id+"F2.wireOp",EDGE,"E35.0.5.0")}),1.0]])]}),makeQuery(id+"F2.imprint","IMPRINT",FACE,{"disambiguationData":[TD([[makeQuery(id+"F2.imprint","IMPRINT",EDGE,{"derivedFrom":sQuery(id+"F2.wireOp",EDGE,"E35.0.6.0")}),1.0]])]}),makeQuery(id+"F2.imprint","IMPRINT",FACE,{"disambiguationData":[TD([[makeQuery(id+"F2.imprint","IMPRINT",EDGE,{"derivedFrom":sQuery(id+"F2.wireOp",EDGE,"E35.0.7.0")}),1.0]])]}),makeQuery(id+"F2.imprint","IMPRINT",FACE,{"disambiguationData":[TD([[makeQuery(id+"F2.imprint","IMPRINT",EDGE,{"derivedFrom":sQuery(id+"F2.wireOp",EDGE,"E35.0.8.0")}),1.0]])]}),makeQuery(id+"F2.imprint","IMPRINT",FACE,{"disambiguationData":[TD([[makeQuery(id+"F2.imprint","IMPRINT",EDGE,{"derivedFrom":sQuery(id+"F2.wireOp",EDGE,"E35.0.9.0")}),1.0]])]}),makeQuery(id+"F2.imprint","IMPRINT",FACE,{"disambiguationData":[TD([[makeQuery(id+"F2.imprint","IMPRINT",EDGE,{"derivedFrom":sQuery(id+"F2.wireOp",EDGE,"E35.0.10.0")}),1.0]])]}),makeQuery(id+"F2.imprint","IMPRINT",FACE,{"disambiguationData":[TD([[makeQuery(id+"F2.imprint","IMPRINT",EDGE,{"derivedFrom":sQuery(id+"F2.wireOp",EDGE,"E35.0.11.0")}),1.0]])]}),makeQuery(id+"F2.imprint","IMPRINT",FACE,{"disambiguationData":[TD([[makeQuery(id+"F2.imprint","IMPRINT",EDGE,{"derivedFrom":sQuery(id+"F2.wireOp",EDGE,"E35.0.12.0")}),1.0]])]}),makeQuery(id+"F2.imprint","IMPRINT",FACE,{"disambiguationData":[TD([[makeQuery(id+"F2.imprint","IMPRINT",EDGE,{"derivedFrom":sQuery(id+"F2.wireOp",EDGE,"E35.0.13.0")}),1.0]])]})]);}
            extrude(context, id + "F3", {"entities" : qUnion([Q0]), "operationType" : NewBodyOperationType.REMOVE, "oppositeDirection" : true, "depth" : 25.4 * mm});
        }
    });
